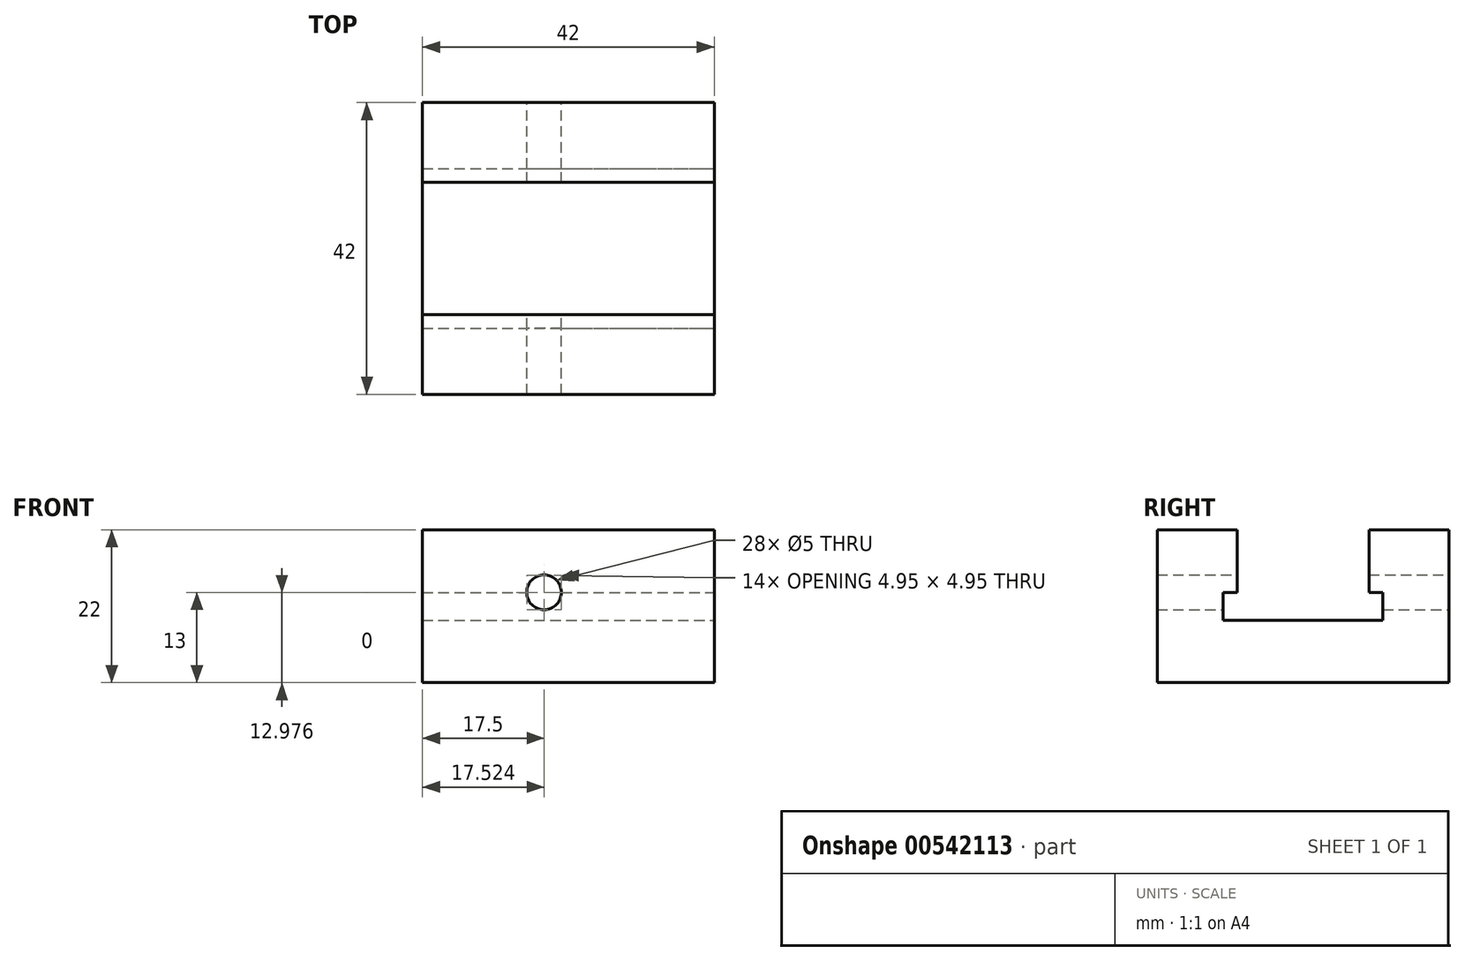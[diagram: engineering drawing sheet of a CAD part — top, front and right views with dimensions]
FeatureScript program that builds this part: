
annotation { "Feature Type Name" : "Feature", "Feature Type Description" : "" }
export const myFeature = defineFeature(function(context is Context, id is Id, definition is map)
    precondition{}
    {
        {
            var Q0;
            Q0=qCreatedBy(makeId("Front.planeOp"),FACE);
            var sketch = newSketch(context, id + "F0", { "sketchPlane" : qUnion([Q0])});
            skLineSegment(sketch, "E0.bottom", {"start": v(21, -13) * mm, "end": v(-21, -13) * mm});
            skLineSegment(sketch, "E0.top", {"start": v(21, 9) * mm, "end": v(-21, 9) * mm});
            skLineSegment(sketch, "E0.left", {"start": v(21, -13) * mm, "end": v(21, 9) * mm});
            skLineSegment(sketch, "E0.right", {"start": v(-21, -13) * mm, "end": v(-21, 9) * mm});
            skPoint(sketch, "E0.middle", {"position": v(0, -2) * mm});
            skLineSegment(sketch, "E1", {"start": v(-21, 9) * mm, "end": v(-3.5, 9) * mm});
            skLineSegment(sketch, "E2", {"start": v(-3.5, 9) * mm, "end": v(-3.5, -13) * mm});
            skLineSegment(sketch, "E3", {"start": v(-3.5, -13) * mm, "end": v(-3.5, 0) * mm});
            skCircle(sketch, "E4", {"center": v(-3.5, 0) * mm, "radius": 2.5 * mm});
            skSolve(sketch);
        }
        {
            var Q0;
            {var subQ1=sQuery(id+"F0.wireOp",EDGE,"E0.right");Q0=makeQuery(id+"F0.imprint","IMPRINT",FACE,{"disambiguationData":[TD([[makeQuery(id+"F0.imprint","IMPRINT",EDGE,{"derivedFrom":subQ1}),-1.0]])]});}
            var Q1;
            {var subQ1=sQuery(id+"F0.wireOp",EDGE,"E0.top");Q1=makeQuery(id+"F0.imprint","IMPRINT",FACE,{"disambiguationData":[TD([[makeQuery(id+"F0.imprint","IMPRINT",EDGE,{"derivedFrom":subQ1}),1.0]])]});}
            extrude(context, id + "F1", {"entities" : qUnion([Q0, Q1]), "depth" : 42 * mm, "offsetDistance" : 25 * mm});
        }
        {
            var Q0;
            Q0=makeQuery(id+"F1.opExtrude","SWEPT_FACE",FACE,{"disambiguationData":[OSD([sQuery(id+"F0.wireOp",EDGE,"E0.left")])]});
            var sketch = newSketch(context, id + "F2", { "sketchPlane" : qUnion([Q0])});
            skLineSegment(sketch, "E5", {"start": v(-21, 9) * mm, "end": v(-21, -13) * mm});
            skLineSegment(sketch, "E6", {"start": v(-21, -13) * mm, "end": v(-21, -4) * mm});
            skLineSegment(sketch, "E7", {"start": v(-21, -4) * mm, "end": v(-9.5, -4) * mm});
            skLineSegment(sketch, "E8", {"start": v(-9.5, -4) * mm, "end": v(-32.5, -4) * mm});
            skPoint(sketch, "E8.endSnap0", {"position": v(-15.25, -4) * mm});
            skLineSegment(sketch, "E9", {"start": v(-32.5, -4) * mm, "end": v(-32.5, 0) * mm});
            skLineSegment(sketch, "E10", {"start": v(-32.5, 0) * mm, "end": v(-9.5, 0) * mm});
            skLineSegment(sketch, "E11", {"start": v(-9.5, 0) * mm, "end": v(-9.5, -4) * mm});
            skLineSegment(sketch, "E12", {"start": v(-32.5, 0) * mm, "end": v(-30.5, 0) * mm});
            skLineSegment(sketch, "E13", {"start": v(-9.5, 0) * mm, "end": v(-11.5, 0) * mm});
            skLineSegment(sketch, "E14", {"start": v(-30.5, 0) * mm, "end": v(-30.5, 9) * mm});
            skLineSegment(sketch, "E15", {"start": v(-30.5, 9) * mm, "end": v(-11.5, 9) * mm});
            skLineSegment(sketch, "E16", {"start": v(-11.5, 9) * mm, "end": v(-11.5, 0) * mm});
            skSolve(sketch);
        }
        {
            var Q0;
            {var subQ5=sQuery(id+"F2.wireOp",EDGE,"E14");Q0=makeQuery(id+"F2.imprint","IMPRINT",FACE,{"disambiguationData":[TD([[makeQuery(id+"F2.imprint","IMPRINT",EDGE,{"derivedFrom":subQ5}),-1.0]])]});}
            var Q1;
            {var subQ5=sQuery(id+"F2.wireOp",EDGE,"E16");Q1=makeQuery(id+"F2.imprint","IMPRINT",FACE,{"disambiguationData":[TD([[makeQuery(id+"F2.imprint","IMPRINT",EDGE,{"derivedFrom":subQ5}),-1.0]])]});}
            var Q2;
            {var subQ0=sQuery(id+"F2.wireOp",EDGE,"E9");Q2=makeQuery(id+"F2.imprint","IMPRINT",FACE,{"disambiguationData":[TD([[makeQuery(id+"F2.imprint","IMPRINT",EDGE,{"derivedFrom":subQ0}),-1.0]])]});}
            var Q3;
            {var subQ4=sQuery(id+"F2.wireOp",EDGE,"E11");Q3=makeQuery(id+"F2.imprint","IMPRINT",FACE,{"disambiguationData":[TD([[makeQuery(id+"F2.imprint","IMPRINT",EDGE,{"derivedFrom":subQ4}),-1.0]])]});}
            extrude(context, id + "F3", {"entities" : qUnion([Q0, Q1, Q2, Q3]), "operationType" : NewBodyOperationType.REMOVE, "oppositeDirection" : true, "depth" : 42 * mm, "offsetDistance" : 25 * mm});
        }
    });
